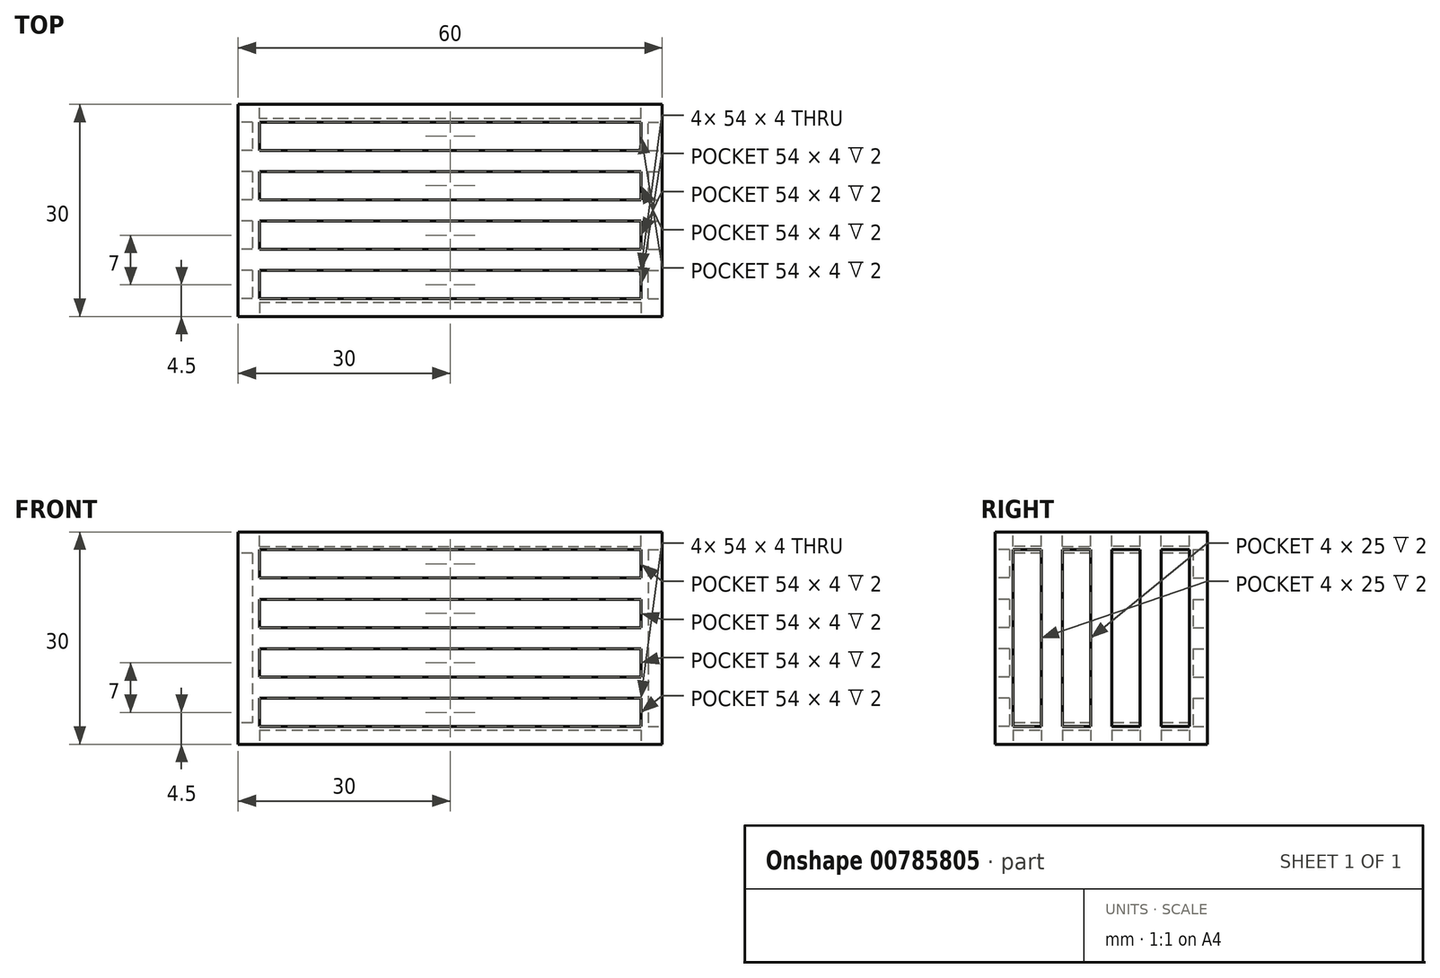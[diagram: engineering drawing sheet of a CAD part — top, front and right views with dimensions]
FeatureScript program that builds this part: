
annotation { "Feature Type Name" : "Feature", "Feature Type Description" : "" }
export const myFeature = defineFeature(function(context is Context, id is Id, definition is map)
    precondition{}
    {
        {
            var Q0;
            Q0=qCreatedBy(makeId("Front.planeOp"),FACE);
            var sketch = newSketch(context, id + "F0", { "sketchPlane" : qUnion([Q0])});
            skLineSegment(sketch, "E0.bottom", {"start": v(-30, 15) * mm, "end": v(30, 15) * mm});
            skLineSegment(sketch, "E0.top", {"start": v(-30, -15) * mm, "end": v(30, -15) * mm});
            skLineSegment(sketch, "E0.left", {"start": v(-30, 15) * mm, "end": v(-30, -15) * mm});
            skLineSegment(sketch, "E0.right", {"start": v(30, 15) * mm, "end": v(30, -15) * mm});
            skSolve(sketch);
        }
        {
            var Q0;
            Q0=makeQuery(id+"F0.imprint","IMPRINT",FACE,{"disambiguationData":[TD([[makeQuery(id+"F0.imprint","IMPRINT",EDGE,{"derivedFrom":sQuery(id+"F0.wireOp",EDGE,"E0.bottom")}),-1.0]])]});
            extrude(context, id + "F1", {"entities" : qUnion([Q0]), "depth" : 30 * mm, "offsetDistance" : 25 * mm});
        }
        {
            var Q0;
            Q0=makeQuery(id+"F1.opExtrude","CAP_FACE",FACE,{"disambiguationData":[OSD([sQuery(id+"F0.wireOp",EDGE,"E0.bottom"),sQuery(id+"F0.wireOp",EDGE,"E0.top"),sQuery(id+"F0.wireOp",EDGE,"E0.left"),sQuery(id+"F0.wireOp",EDGE,"E0.right")])],"isStart":false});
            var sketch = newSketch(context, id + "F2", { "sketchPlane" : qUnion([Q0])});
            skLineSegment(sketch, "E1", {"start": v(0, -15) * mm, "end": v(0, 15) * mm, "construction": true});
            skLineSegment(sketch, "E2.bottom", {"start": v(-27, 12.5) * mm, "end": v(27, 12.5) * mm});
            skLineSegment(sketch, "E2.top", {"start": v(-27, 8.5) * mm, "end": v(27, 8.5) * mm});
            skLineSegment(sketch, "E2.left", {"start": v(-27, 12.5) * mm, "end": v(-27, 8.5) * mm});
            skLineSegment(sketch, "E2.right", {"start": v(27, 12.5) * mm, "end": v(27, 8.5) * mm});
            skLineSegment(sketch, "E3.bottom", {"start": v(-27, 5.5) * mm, "end": v(27, 5.5) * mm});
            skLineSegment(sketch, "E3.top", {"start": v(-27, 1.5) * mm, "end": v(27, 1.5) * mm});
            skLineSegment(sketch, "E3.left", {"start": v(-27, 5.5) * mm, "end": v(-27, 1.5) * mm});
            skLineSegment(sketch, "E3.right", {"start": v(27, 5.5) * mm, "end": v(27, 1.5) * mm});
            skLineSegment(sketch, "E4.bottom", {"start": v(-27, -1.5) * mm, "end": v(27, -1.5) * mm});
            skLineSegment(sketch, "E4.top", {"start": v(-27, -5.5) * mm, "end": v(27, -5.5) * mm});
            skLineSegment(sketch, "E4.left", {"start": v(-27, -1.5) * mm, "end": v(-27, -5.5) * mm});
            skLineSegment(sketch, "E4.right", {"start": v(27, -1.5) * mm, "end": v(27, -5.5) * mm});
            skLineSegment(sketch, "E5.bottom", {"start": v(-27, -8.5) * mm, "end": v(27, -8.5) * mm});
            skLineSegment(sketch, "E5.top", {"start": v(-27, -12.5) * mm, "end": v(27, -12.5) * mm});
            skLineSegment(sketch, "E5.left", {"start": v(-27, -8.5) * mm, "end": v(-27, -12.5) * mm});
            skLineSegment(sketch, "E5.right", {"start": v(27, -8.5) * mm, "end": v(27, -12.5) * mm});
            skSolve(sketch);
        }
        {
            var Q0;
            Q0=makeQuery(id+"F2.imprint","IMPRINT",FACE,{"disambiguationData":[TD([[makeQuery(id+"F2.imprint","IMPRINT",EDGE,{"derivedFrom":sQuery(id+"F2.wireOp",EDGE,"E5.bottom")}),-1.0]])]});
            var Q1;
            Q1=makeQuery(id+"F2.imprint","IMPRINT",FACE,{"disambiguationData":[TD([[makeQuery(id+"F2.imprint","IMPRINT",EDGE,{"derivedFrom":sQuery(id+"F2.wireOp",EDGE,"E4.bottom")}),-1.0]])]});
            var Q2;
            Q2=makeQuery(id+"F2.imprint","IMPRINT",FACE,{"disambiguationData":[TD([[makeQuery(id+"F2.imprint","IMPRINT",EDGE,{"derivedFrom":sQuery(id+"F2.wireOp",EDGE,"E3.bottom")}),-1.0]])]});
            var Q3;
            Q3=makeQuery(id+"F2.imprint","IMPRINT",FACE,{"disambiguationData":[TD([[makeQuery(id+"F2.imprint","IMPRINT",EDGE,{"derivedFrom":sQuery(id+"F2.wireOp",EDGE,"E2.bottom")}),-1.0]])]});
            extrude(context, id + "F3", {"entities" : qUnion([Q0, Q1, Q2, Q3]), "operationType" : NewBodyOperationType.REMOVE, "oppositeDirection" : true, "depth" : 2 * mm, "offsetDistance" : 25 * mm});
        }
        {
            var Q0;
            Q0=makeQuery(id+"F1.opExtrude","SWEPT_FACE",FACE,{"disambiguationData":[OSD([sQuery(id+"F0.wireOp",EDGE,"E0.bottom")])]});
            var sketch = newSketch(context, id + "F4", { "sketchPlane" : qUnion([Q0])});
            skLineSegment(sketch, "E6.bottom", {"start": v(-27, -2.5) * mm, "end": v(27, -2.5) * mm});
            skLineSegment(sketch, "E6.top", {"start": v(-27, -6.5) * mm, "end": v(27, -6.5) * mm});
            skLineSegment(sketch, "E6.left", {"start": v(-27, -2.5) * mm, "end": v(-27, -6.5) * mm});
            skLineSegment(sketch, "E6.right", {"start": v(27, -2.5) * mm, "end": v(27, -6.5) * mm});
            skLineSegment(sketch, "E7.bottom", {"start": v(-27, -9.5) * mm, "end": v(27, -9.5) * mm});
            skLineSegment(sketch, "E7.top", {"start": v(-27, -13.5) * mm, "end": v(27, -13.5) * mm});
            skLineSegment(sketch, "E7.left", {"start": v(-27, -9.5) * mm, "end": v(-27, -13.5) * mm});
            skLineSegment(sketch, "E7.right", {"start": v(27, -9.5) * mm, "end": v(27, -13.5) * mm});
            skLineSegment(sketch, "E8", {"start": v(0, -30) * mm, "end": v(0, 0) * mm, "construction": true});
            skPoint(sketch, "E9.firstSnap0", {"position": v(-30, -15) * mm});
            skLineSegment(sketch, "E9.top", {"start": v(-27, -20.5) * mm, "end": v(27, -20.5) * mm});
            skLineSegment(sketch, "E9.right", {"start": v(27, -16.5) * mm, "end": v(27, -20.5) * mm});
            skLineSegment(sketch, "E10", {"start": v(27, -16.5) * mm, "end": v(-27, -16.5) * mm});
            skLineSegment(sketch, "E11", {"start": v(-27, -20.5) * mm, "end": v(-27, -16.5) * mm});
            skLineSegment(sketch, "E12.bottom", {"start": v(-27, -23.5) * mm, "end": v(27, -23.5) * mm});
            skLineSegment(sketch, "E12.top", {"start": v(-27, -27.5) * mm, "end": v(27, -27.5) * mm});
            skLineSegment(sketch, "E12.left", {"start": v(-27, -23.5) * mm, "end": v(-27, -27.5) * mm});
            skLineSegment(sketch, "E12.right", {"start": v(27, -23.5) * mm, "end": v(27, -27.5) * mm});
            skSolve(sketch);
        }
        {
            var Q0;
            Q0=makeQuery(id+"F4.imprint","IMPRINT",FACE,{"disambiguationData":[TD([[makeQuery(id+"F4.imprint","IMPRINT",EDGE,{"derivedFrom":sQuery(id+"F4.wireOp",EDGE,"E6.bottom")}),-1.0]])]});
            var Q1;
            Q1=makeQuery(id+"F4.imprint","IMPRINT",FACE,{"disambiguationData":[TD([[makeQuery(id+"F4.imprint","IMPRINT",EDGE,{"derivedFrom":sQuery(id+"F4.wireOp",EDGE,"E7.bottom")}),-1.0]])]});
            var Q2;
            Q2=makeQuery(id+"F4.imprint","IMPRINT",FACE,{"disambiguationData":[TD([[makeQuery(id+"F4.imprint","IMPRINT",EDGE,{"derivedFrom":sQuery(id+"F4.wireOp",EDGE,"E9.top")}),1.0]])]});
            var Q3;
            Q3=makeQuery(id+"F4.imprint","IMPRINT",FACE,{"disambiguationData":[TD([[makeQuery(id+"F4.imprint","IMPRINT",EDGE,{"derivedFrom":sQuery(id+"F4.wireOp",EDGE,"E12.bottom")}),-1.0]])]});
            extrude(context, id + "F5", {"entities" : qUnion([Q0, Q1, Q2, Q3]), "operationType" : NewBodyOperationType.REMOVE, "oppositeDirection" : true, "depth" : 2 * mm, "offsetDistance" : 25 * mm});
        }
        {
            var Q0;
            Q0=makeQuery(id+"F1.opExtrude","CAP_FACE",FACE,{"disambiguationData":[OSD([sQuery(id+"F0.wireOp",EDGE,"E0.bottom"),sQuery(id+"F0.wireOp",EDGE,"E0.top"),sQuery(id+"F0.wireOp",EDGE,"E0.left"),sQuery(id+"F0.wireOp",EDGE,"E0.right")])],"isStart":true});
            var sketch = newSketch(context, id + "F6", { "sketchPlane" : qUnion([Q0])});
            skLineSegment(sketch, "E13.bottom", {"start": v(-27, 12.5) * mm, "end": v(27, 12.5) * mm});
            skLineSegment(sketch, "E13.top", {"start": v(-27, 8.5) * mm, "end": v(27, 8.5) * mm});
            skLineSegment(sketch, "E13.left", {"start": v(-27, 12.5) * mm, "end": v(-27, 8.5) * mm});
            skLineSegment(sketch, "E13.right", {"start": v(27, 12.5) * mm, "end": v(27, 8.5) * mm});
            skLineSegment(sketch, "E14.bottom", {"start": v(-27, 5.5) * mm, "end": v(27, 5.5) * mm});
            skLineSegment(sketch, "E14.top", {"start": v(-27, 1.5) * mm, "end": v(27, 1.5) * mm});
            skLineSegment(sketch, "E14.left", {"start": v(-27, 5.5) * mm, "end": v(-27, 1.5) * mm});
            skLineSegment(sketch, "E14.right", {"start": v(27, 5.5) * mm, "end": v(27, 1.5) * mm});
            skLineSegment(sketch, "E15.bottom", {"start": v(-27, -1.5) * mm, "end": v(27, -1.5) * mm});
            skLineSegment(sketch, "E15.top", {"start": v(-27, -5.5) * mm, "end": v(27, -5.5) * mm});
            skLineSegment(sketch, "E15.left", {"start": v(-27, -1.5) * mm, "end": v(-27, -5.5) * mm});
            skLineSegment(sketch, "E15.right", {"start": v(27, -1.5) * mm, "end": v(27, -5.5) * mm});
            skLineSegment(sketch, "E16.bottom", {"start": v(-27, -8.5) * mm, "end": v(27, -8.5) * mm});
            skLineSegment(sketch, "E16.top", {"start": v(-27, -12.5) * mm, "end": v(27, -12.5) * mm});
            skLineSegment(sketch, "E16.left", {"start": v(-27, -8.5) * mm, "end": v(-27, -12.5) * mm});
            skLineSegment(sketch, "E16.right", {"start": v(27, -8.5) * mm, "end": v(27, -12.5) * mm});
            skLineSegment(sketch, "E17", {"start": v(0, -15) * mm, "end": v(0, 15) * mm, "construction": true});
            skSolve(sketch);
        }
        {
            var Q0;
            Q0=makeQuery(id+"F6.imprint","IMPRINT",FACE,{"disambiguationData":[TD([[makeQuery(id+"F6.imprint","IMPRINT",EDGE,{"derivedFrom":sQuery(id+"F6.wireOp",EDGE,"E13.bottom")}),-1.0]])]});
            var Q1;
            Q1=makeQuery(id+"F6.imprint","IMPRINT",FACE,{"disambiguationData":[TD([[makeQuery(id+"F6.imprint","IMPRINT",EDGE,{"derivedFrom":sQuery(id+"F6.wireOp",EDGE,"E14.bottom")}),-1.0]])]});
            var Q2;
            Q2=makeQuery(id+"F6.imprint","IMPRINT",FACE,{"disambiguationData":[TD([[makeQuery(id+"F6.imprint","IMPRINT",EDGE,{"derivedFrom":sQuery(id+"F6.wireOp",EDGE,"E15.bottom")}),-1.0]])]});
            var Q3;
            Q3=makeQuery(id+"F6.imprint","IMPRINT",FACE,{"disambiguationData":[TD([[makeQuery(id+"F6.imprint","IMPRINT",EDGE,{"derivedFrom":sQuery(id+"F6.wireOp",EDGE,"E16.bottom")}),-1.0]])]});
            extrude(context, id + "F7", {"entities" : qUnion([Q0, Q1, Q2, Q3]), "operationType" : NewBodyOperationType.REMOVE, "oppositeDirection" : true, "depth" : 2 * mm, "offsetDistance" : 25 * mm});
        }
        {
            var Q0;
            Q0=makeQuery(id+"F1.opExtrude","SWEPT_FACE",FACE,{"disambiguationData":[OSD([sQuery(id+"F0.wireOp",EDGE,"E0.top")])]});
            var sketch = newSketch(context, id + "F8", { "sketchPlane" : qUnion([Q0])});
            skLineSegment(sketch, "E18.bottom", {"start": v(-27, 27.5) * mm, "end": v(27, 27.5) * mm});
            skLineSegment(sketch, "E18.top", {"start": v(-27, 23.5) * mm, "end": v(27, 23.5) * mm});
            skLineSegment(sketch, "E18.left", {"start": v(-27, 27.5) * mm, "end": v(-27, 23.5) * mm});
            skLineSegment(sketch, "E18.right", {"start": v(27, 27.5) * mm, "end": v(27, 23.5) * mm});
            skLineSegment(sketch, "E19.bottom", {"start": v(-27, 20.5) * mm, "end": v(27, 20.5) * mm});
            skLineSegment(sketch, "E19.top", {"start": v(-27, 16.5) * mm, "end": v(27, 16.5) * mm});
            skLineSegment(sketch, "E19.left", {"start": v(-27, 20.5) * mm, "end": v(-27, 16.5) * mm});
            skLineSegment(sketch, "E19.right", {"start": v(27, 20.5) * mm, "end": v(27, 16.5) * mm});
            skLineSegment(sketch, "E20.bottom", {"start": v(-27, 13.5) * mm, "end": v(27, 13.5) * mm});
            skLineSegment(sketch, "E20.top", {"start": v(-27, 9.5) * mm, "end": v(27, 9.5) * mm});
            skLineSegment(sketch, "E20.left", {"start": v(-27, 13.5) * mm, "end": v(-27, 9.5) * mm});
            skLineSegment(sketch, "E20.right", {"start": v(27, 13.5) * mm, "end": v(27, 9.5) * mm});
            skLineSegment(sketch, "E21.bottom", {"start": v(-27, 6.5) * mm, "end": v(27, 6.5) * mm});
            skLineSegment(sketch, "E21.top", {"start": v(-27, 2.5) * mm, "end": v(27, 2.5) * mm});
            skLineSegment(sketch, "E21.left", {"start": v(-27, 6.5) * mm, "end": v(-27, 2.5) * mm});
            skLineSegment(sketch, "E21.right", {"start": v(27, 6.5) * mm, "end": v(27, 2.5) * mm});
            skLineSegment(sketch, "E22", {"start": v(0, 0) * mm, "end": v(0, 30) * mm, "construction": true});
            skSolve(sketch);
        }
        {
            var Q0;
            Q0=makeQuery(id+"F8.imprint","IMPRINT",FACE,{"disambiguationData":[TD([[makeQuery(id+"F8.imprint","IMPRINT",EDGE,{"derivedFrom":sQuery(id+"F8.wireOp",EDGE,"E18.bottom")}),-1.0]])]});
            var Q1;
            Q1=makeQuery(id+"F8.imprint","IMPRINT",FACE,{"disambiguationData":[TD([[makeQuery(id+"F8.imprint","IMPRINT",EDGE,{"derivedFrom":sQuery(id+"F8.wireOp",EDGE,"E19.bottom")}),-1.0]])]});
            var Q2;
            Q2=makeQuery(id+"F8.imprint","IMPRINT",FACE,{"disambiguationData":[TD([[makeQuery(id+"F8.imprint","IMPRINT",EDGE,{"derivedFrom":sQuery(id+"F8.wireOp",EDGE,"E20.bottom")}),-1.0]])]});
            var Q3;
            Q3=makeQuery(id+"F8.imprint","IMPRINT",FACE,{"disambiguationData":[TD([[makeQuery(id+"F8.imprint","IMPRINT",EDGE,{"derivedFrom":sQuery(id+"F8.wireOp",EDGE,"E21.bottom")}),-1.0]])]});
            extrude(context, id + "F9", {"entities" : qUnion([Q0, Q1, Q2, Q3]), "operationType" : NewBodyOperationType.REMOVE, "oppositeDirection" : true, "depth" : 2 * mm, "offsetDistance" : 25 * mm});
        }
        {
            var Q0;
            Q0=makeQuery(id+"F1.opExtrude","SWEPT_FACE",FACE,{"disambiguationData":[OSD([sQuery(id+"F0.wireOp",EDGE,"E0.left")])]});
            var sketch = newSketch(context, id + "F10", { "sketchPlane" : qUnion([Q0])});
            skLineSegment(sketch, "E23.bottom", {"start": v(2.5, -12) * mm, "end": v(6.5, -12) * mm});
            skLineSegment(sketch, "E23.top", {"start": v(2.5, 12) * mm, "end": v(6.5, 12) * mm});
            skLineSegment(sketch, "E23.left", {"start": v(2.5, -12) * mm, "end": v(2.5, 12) * mm});
            skLineSegment(sketch, "E23.right", {"start": v(6.5, -12) * mm, "end": v(6.5, 12) * mm});
            skLineSegment(sketch, "E24.bottom", {"start": v(9.5, 12) * mm, "end": v(13.5, 12) * mm});
            skLineSegment(sketch, "E24.top", {"start": v(9.5, -12) * mm, "end": v(13.5, -12) * mm});
            skLineSegment(sketch, "E24.left", {"start": v(9.5, 12) * mm, "end": v(9.5, -12) * mm});
            skLineSegment(sketch, "E24.right", {"start": v(13.5, 12) * mm, "end": v(13.5, -12) * mm});
            skLineSegment(sketch, "E25.bottom", {"start": v(23.5, 12) * mm, "end": v(27.5, 12) * mm});
            skLineSegment(sketch, "E25.top", {"start": v(23.5, -12) * mm, "end": v(27.5, -12) * mm});
            skLineSegment(sketch, "E25.left", {"start": v(23.5, 12) * mm, "end": v(23.5, -12) * mm});
            skLineSegment(sketch, "E25.right", {"start": v(27.5, 12) * mm, "end": v(27.5, -12) * mm});
            skLineSegment(sketch, "E26.bottom", {"start": v(16.5, 12) * mm, "end": v(20.5, 12) * mm});
            skLineSegment(sketch, "E26.top", {"start": v(16.5, -12) * mm, "end": v(20.5, -12) * mm});
            skLineSegment(sketch, "E26.left", {"start": v(16.5, 12) * mm, "end": v(16.5, -12) * mm});
            skLineSegment(sketch, "E26.right", {"start": v(20.5, 12) * mm, "end": v(20.5, -12) * mm});
            skLineSegment(sketch, "E27", {"start": v(30, 0) * mm, "end": v(0, 0) * mm, "construction": true});
            skSolve(sketch);
        }
        {
            var Q0;
            Q0=makeQuery(id+"F10.imprint","IMPRINT",FACE,{"disambiguationData":[TD([[makeQuery(id+"F10.imprint","IMPRINT",EDGE,{"derivedFrom":sQuery(id+"F10.wireOp",EDGE,"E23.bottom")}),1.0]])]});
            var Q1;
            Q1=makeQuery(id+"F10.imprint","IMPRINT",FACE,{"disambiguationData":[TD([[makeQuery(id+"F10.imprint","IMPRINT",EDGE,{"derivedFrom":sQuery(id+"F10.wireOp",EDGE,"E24.bottom")}),-1.0]])]});
            var Q2;
            Q2=makeQuery(id+"F10.imprint","IMPRINT",FACE,{"disambiguationData":[TD([[makeQuery(id+"F10.imprint","IMPRINT",EDGE,{"derivedFrom":sQuery(id+"F10.wireOp",EDGE,"E26.bottom")}),-1.0]])]});
            var Q3;
            Q3=makeQuery(id+"F10.imprint","IMPRINT",FACE,{"disambiguationData":[TD([[makeQuery(id+"F10.imprint","IMPRINT",EDGE,{"derivedFrom":sQuery(id+"F10.wireOp",EDGE,"E25.bottom")}),-1.0]])]});
            extrude(context, id + "F11", {"entities" : qUnion([Q0, Q1, Q2, Q3]), "operationType" : NewBodyOperationType.REMOVE, "oppositeDirection" : true, "depth" : 2 * mm, "offsetDistance" : 25 * mm});
        }
        {
            var Q0;
            Q0=makeQuery(id+"F1.opExtrude","SWEPT_FACE",FACE,{"disambiguationData":[OSD([sQuery(id+"F0.wireOp",EDGE,"E0.right")])]});
            var sketch = newSketch(context, id + "F12", { "sketchPlane" : qUnion([Q0])});
            skLineSegment(sketch, "E28", {"start": v(-30, 0) * mm, "end": v(0, 0) * mm, "construction": true});
            skLineSegment(sketch, "E29.bottom", {"start": v(-27.5, 12.5) * mm, "end": v(-23.5, 12.5) * mm});
            skLineSegment(sketch, "E29.top", {"start": v(-27.5, -12.5) * mm, "end": v(-23.5, -12.5) * mm});
            skLineSegment(sketch, "E29.left", {"start": v(-27.5, 12.5) * mm, "end": v(-27.5, -12.5) * mm});
            skLineSegment(sketch, "E29.right", {"start": v(-23.5, 12.5) * mm, "end": v(-23.5, -12.5) * mm});
            skLineSegment(sketch, "E30.bottom", {"start": v(-20.5, 12.5) * mm, "end": v(-16.5, 12.5) * mm});
            skLineSegment(sketch, "E30.top", {"start": v(-20.5, -12.5) * mm, "end": v(-16.5, -12.5) * mm});
            skLineSegment(sketch, "E30.left", {"start": v(-20.5, 12.5) * mm, "end": v(-20.5, -12.5) * mm});
            skLineSegment(sketch, "E30.right", {"start": v(-16.5, 12.5) * mm, "end": v(-16.5, -12.5) * mm});
            skLineSegment(sketch, "E31.bottom", {"start": v(-9.5, 12.5) * mm, "end": v(-13.5, 12.5) * mm});
            skLineSegment(sketch, "E31.top", {"start": v(-9.5, -12.5) * mm, "end": v(-13.5, -12.5) * mm});
            skLineSegment(sketch, "E31.left", {"start": v(-9.5, 12.5) * mm, "end": v(-9.5, -12.5) * mm});
            skLineSegment(sketch, "E31.right", {"start": v(-13.5, 12.5) * mm, "end": v(-13.5, -12.5) * mm});
            skLineSegment(sketch, "E32.bottom", {"start": v(-6.5, 12.5) * mm, "end": v(-2.5, 12.5) * mm});
            skLineSegment(sketch, "E32.top", {"start": v(-6.5, -12.5) * mm, "end": v(-2.5, -12.5) * mm});
            skLineSegment(sketch, "E32.left", {"start": v(-6.5, 12.5) * mm, "end": v(-6.5, -12.5) * mm});
            skLineSegment(sketch, "E32.right", {"start": v(-2.5, 12.5) * mm, "end": v(-2.5, -12.5) * mm});
            skSolve(sketch);
        }
        {
            var Q0;
            Q0=makeQuery(id+"F12.imprint","IMPRINT",FACE,{"disambiguationData":[TD([[makeQuery(id+"F12.imprint","IMPRINT",EDGE,{"derivedFrom":sQuery(id+"F12.wireOp",EDGE,"E29.bottom")}),-1.0]])]});
            var Q1;
            Q1=makeQuery(id+"F12.imprint","IMPRINT",FACE,{"disambiguationData":[TD([[makeQuery(id+"F12.imprint","IMPRINT",EDGE,{"derivedFrom":sQuery(id+"F12.wireOp",EDGE,"E30.bottom")}),-1.0]])]});
            var Q2;
            Q2=makeQuery(id+"F12.imprint","IMPRINT",FACE,{"disambiguationData":[TD([[makeQuery(id+"F12.imprint","IMPRINT",EDGE,{"derivedFrom":sQuery(id+"F12.wireOp",EDGE,"E31.bottom")}),1.0]])]});
            var Q3;
            Q3=makeQuery(id+"F12.imprint","IMPRINT",FACE,{"disambiguationData":[TD([[makeQuery(id+"F12.imprint","IMPRINT",EDGE,{"derivedFrom":sQuery(id+"F12.wireOp",EDGE,"E32.bottom")}),-1.0]])]});
            extrude(context, id + "F13", {"entities" : qUnion([Q0, Q1, Q2, Q3]), "operationType" : NewBodyOperationType.REMOVE, "oppositeDirection" : true, "depth" : 2 * mm, "offsetDistance" : 25 * mm});
        }
    });
